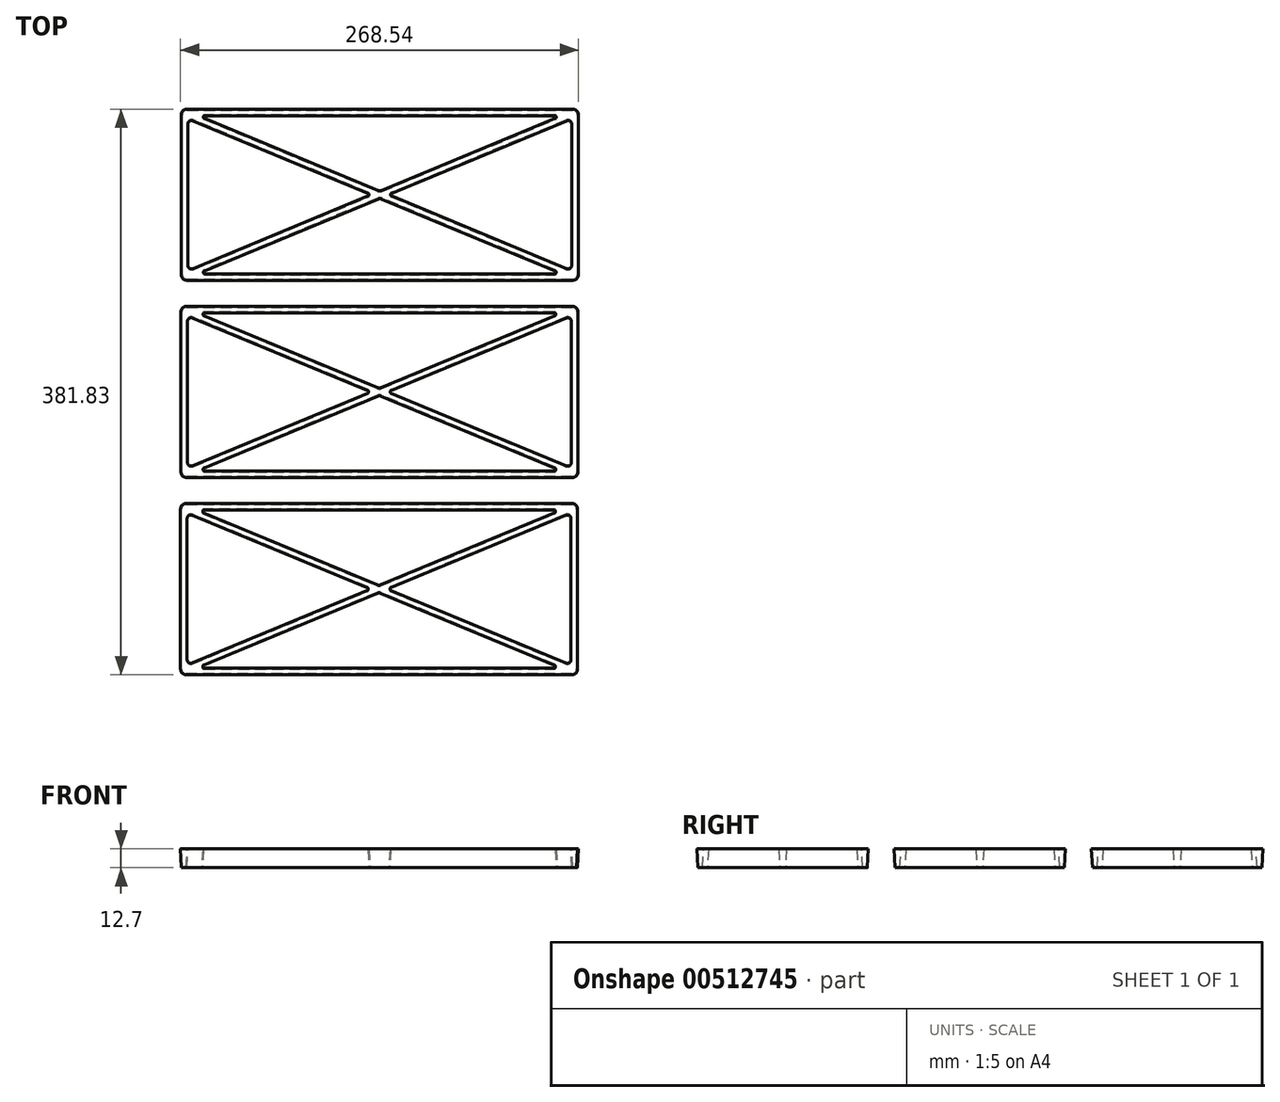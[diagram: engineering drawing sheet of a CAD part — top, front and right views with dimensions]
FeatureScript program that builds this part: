
annotation { "Feature Type Name" : "Feature", "Feature Type Description" : "" }
export const myFeature = defineFeature(function(context is Context, id is Id, definition is map)
    precondition{}
    {
        {
            var Q0;
            Q0=qCreatedBy(makeId("Top.planeOp"),FACE);
            var sketch = newSketch(context, id + "F0", { "sketchPlane" : qUnion([Q0])});
            skLineSegment(sketch, "E0.bottom", {"start": v(-3.18, 0) * mm, "end": v(-263.53, 0) * mm});
            skLineSegment(sketch, "E0.top", {"start": v(-3.18, 114.3) * mm, "end": v(-263.53, 114.3) * mm});
            skLineSegment(sketch, "E0.left", {"start": v(0, 3.17) * mm, "end": v(0, 111.13) * mm});
            skLineSegment(sketch, "E0.right", {"start": v(-266.7, 3.18) * mm, "end": v(-266.7, 111.12) * mm});
            skLineSegment(sketch, "E1.0", {"start": v(-15.3, 111.13) * mm, "end": v(-251.4, 111.13) * mm});
            skLineSegment(sketch, "E2.0", {"start": v(-263.53, 9.65) * mm, "end": v(-263.53, 104.65) * mm});
            skLineSegment(sketch, "E3.0", {"start": v(-15.3, 3.18) * mm, "end": v(-251.4, 3.17) * mm});
            skLineSegment(sketch, "E4.0", {"start": v(-3.18, 9.65) * mm, "end": v(-3.18, 104.65) * mm});
            skLineSegment(sketch, "E5", {"start": v(-263.53, 111.13) * mm, "end": v(-3.18, 3.18) * mm});
            skLineSegment(sketch, "E6", {"start": v(-3.17, 111.13) * mm, "end": v(-263.53, 3.17) * mm});
            skLineSegment(sketch, "E7.0", {"start": v(-132.13, 54.93) * mm, "end": v(-14.69, 6.23) * mm});
            skLineSegment(sketch, "E8.0", {"start": v(-252.01, 108.07) * mm, "end": v(-134.57, 59.37) * mm});
            skLineSegment(sketch, "E9.0", {"start": v(-14.69, 108.07) * mm, "end": v(-132.13, 59.37) * mm});
            skLineSegment(sketch, "E10.0", {"start": v(-134.57, 54.93) * mm, "end": v(-252.01, 6.23) * mm});
            skArc(sketch, "E11.filletArc", {"start": v(-259.13, 107.59) * mm, "mid": v(-262.11, 107.3) * mm, "end": v(-263.53, 104.65) * mm});
            skArc(sketch, "E12.filletArc", {"start": v(-251.4, 111.13) * mm, "mid": v(-252.96, 109.85) * mm, "end": v(-252.01, 108.07) * mm});
            skArc(sketch, "E13.filletArc", {"start": v(-252.01, 6.23) * mm, "mid": v(-252.96, 4.45) * mm, "end": v(-251.4, 3.17) * mm});
            skPoint(sketch, "E14.newPointA", {"position": v(0, 3.18) * mm});
            skArc(sketch, "E14.filletArc", {"start": v(-15.3, 3.18) * mm, "mid": v(-13.74, 4.45) * mm, "end": v(-14.69, 6.23) * mm});
            skArc(sketch, "E15.filletArc", {"start": v(-3.18, 104.65) * mm, "mid": v(-4.59, 107.3) * mm, "end": v(-7.57, 107.59) * mm});
            skPoint(sketch, "E16.newPointB", {"position": v(0, 111.13) * mm});
            skArc(sketch, "E16.filletArc", {"start": v(-14.69, 108.07) * mm, "mid": v(-13.74, 109.85) * mm, "end": v(-15.3, 111.13) * mm});
            skArc(sketch, "E17.filletArc", {"start": v(-263.53, 9.65) * mm, "mid": v(-262.11, 7) * mm, "end": v(-259.13, 6.71) * mm});
            skArc(sketch, "E18.filletArc", {"start": v(-7.57, 6.71) * mm, "mid": v(-4.59, 7) * mm, "end": v(-3.18, 9.65) * mm});
            skArc(sketch, "E19.filletArc", {"start": v(-132.13, 54.93) * mm, "mid": v(-133.35, 55.17) * mm, "end": v(-134.57, 54.93) * mm});
            skArc(sketch, "E20.filletArc", {"start": v(-134.57, 59.37) * mm, "mid": v(-133.35, 59.13) * mm, "end": v(-132.13, 59.37) * mm});
            skLineSegment(sketch, "E21", {"start": v(-259.13, 107.59) * mm, "end": v(-141.03, 58.62) * mm});
            skLineSegment(sketch, "E22", {"start": v(-7.57, 107.59) * mm, "end": v(-125.67, 58.62) * mm});
            skLineSegment(sketch, "E23", {"start": v(-125.67, 55.68) * mm, "end": v(-7.57, 6.71) * mm});
            skLineSegment(sketch, "E24", {"start": v(-259.13, 6.71) * mm, "end": v(-141.03, 55.68) * mm});
            skArc(sketch, "E25.filletArc", {"start": v(-141.03, 55.68) * mm, "mid": v(-140.05, 57.15) * mm, "end": v(-141.03, 58.62) * mm});
            skArc(sketch, "E26.filletArc", {"start": v(-125.67, 58.62) * mm, "mid": v(-126.65, 57.15) * mm, "end": v(-125.67, 55.68) * mm});
            skPoint(sketch, "E27.visualSharp", {"position": v(-266.7, 114.3) * mm});
            skArc(sketch, "E27.filletArc", {"start": v(-263.53, 114.3) * mm, "mid": v(-265.77, 113.37) * mm, "end": v(-266.7, 111.12) * mm});
            skPoint(sketch, "E28.visualSharp", {"position": v(0, 114.3) * mm});
            skArc(sketch, "E28.filletArc", {"start": v(0, 111.13) * mm, "mid": v(-0.93, 113.37) * mm, "end": v(-3.18, 114.3) * mm});
            skPoint(sketch, "E29.visualSharp", {"position": v(0, 0) * mm});
            skArc(sketch, "E29.filletArc", {"start": v(-3.18, 0) * mm, "mid": v(-0.93, 0.93) * mm, "end": v(0, 3.17) * mm});
            skPoint(sketch, "E30.visualSharp", {"position": v(-266.7, 0) * mm});
            skArc(sketch, "E30.filletArc", {"start": v(-266.7, 3.18) * mm, "mid": v(-265.77, 0.93) * mm, "end": v(-263.53, 0) * mm});
            skLineSegment(sketch, "E31.1.0.0", {"start": v(-3.43, -133.1) * mm, "end": v(-263.78, -133.1) * mm});
            skLineSegment(sketch, "E31.1.0.1", {"start": v(-3.43, -18.8) * mm, "end": v(-263.78, -18.8) * mm});
            skLineSegment(sketch, "E31.1.0.2", {"start": v(-259.39, -25.51) * mm, "end": v(-141.29, -74.48) * mm});
            skLineSegment(sketch, "E31.1.0.3", {"start": v(-125.92, -77.41) * mm, "end": v(-7.82, -126.38) * mm});
            skPoint(sketch, "E31.1.0.4", {"position": v(-0.25, -133.1) * mm});
            skLineSegment(sketch, "E31.1.0.5", {"start": v(-259.39, -126.38) * mm, "end": v(-141.29, -77.41) * mm});
            skLineSegment(sketch, "E31.1.0.6", {"start": v(-7.82, -25.51) * mm, "end": v(-125.92, -74.48) * mm});
            skLineSegment(sketch, "E31.1.0.7", {"start": v(-0.25, -129.92) * mm, "end": v(-0.25, -21.97) * mm});
            skLineSegment(sketch, "E31.1.0.8", {"start": v(-132.39, -78.17) * mm, "end": v(-14.94, -126.87) * mm});
            skLineSegment(sketch, "E31.1.0.9", {"start": v(-3.43, -21.97) * mm, "end": v(-263.78, -129.92) * mm});
            skLineSegment(sketch, "E31.1.0.10", {"start": v(-252.27, -25.02) * mm, "end": v(-134.82, -73.72) * mm});
            skLineSegment(sketch, "E31.1.0.11", {"start": v(-266.95, -129.92) * mm, "end": v(-266.95, -21.97) * mm});
            skLineSegment(sketch, "E31.1.0.12", {"start": v(-15.55, -21.97) * mm, "end": v(-251.66, -21.97) * mm});
            skLineSegment(sketch, "E31.1.0.13", {"start": v(-15.55, -129.92) * mm, "end": v(-251.66, -129.92) * mm});
            skPoint(sketch, "E31.1.0.14", {"position": v(-266.95, -133.1) * mm});
            skLineSegment(sketch, "E31.1.0.15", {"start": v(-263.78, -123.45) * mm, "end": v(-263.78, -28.44) * mm});
            skLineSegment(sketch, "E31.1.0.16", {"start": v(-134.82, -78.17) * mm, "end": v(-252.27, -126.87) * mm});
            skLineSegment(sketch, "E31.1.0.17", {"start": v(-3.43, -123.45) * mm, "end": v(-3.43, -28.44) * mm});
            skLineSegment(sketch, "E31.1.0.18", {"start": v(-263.78, -21.97) * mm, "end": v(-3.43, -129.92) * mm});
            skLineSegment(sketch, "E31.1.0.19", {"start": v(-14.94, -25.02) * mm, "end": v(-132.39, -73.72) * mm});
            skPoint(sketch, "E31.1.0.20", {"position": v(-266.95, -18.8) * mm});
            skPoint(sketch, "E31.1.0.21", {"position": v(-0.25, -18.8) * mm});
            skPoint(sketch, "E31.1.0.22", {"position": v(-0.25, -21.97) * mm});
            skPoint(sketch, "E31.1.0.23", {"position": v(-0.25, -129.92) * mm});
            skArc(sketch, "E31.1.0.24", {"start": v(-251.66, -21.97) * mm, "mid": v(-253.22, -23.25) * mm, "end": v(-252.27, -25.02) * mm});
            skArc(sketch, "E31.1.0.25", {"start": v(-259.39, -25.51) * mm, "mid": v(-262.37, -25.8) * mm, "end": v(-263.78, -28.44) * mm});
            skArc(sketch, "E31.1.0.26", {"start": v(-7.82, -126.38) * mm, "mid": v(-4.84, -126.09) * mm, "end": v(-3.43, -123.45) * mm});
            skArc(sketch, "E31.1.0.27", {"start": v(-14.94, -25.02) * mm, "mid": v(-14, -23.25) * mm, "end": v(-15.55, -21.97) * mm});
            skArc(sketch, "E31.1.0.28", {"start": v(-3.43, -28.44) * mm, "mid": v(-4.84, -25.8) * mm, "end": v(-7.82, -25.51) * mm});
            skArc(sketch, "E31.1.0.29", {"start": v(-252.27, -126.87) * mm, "mid": v(-253.22, -128.64) * mm, "end": v(-251.66, -129.92) * mm});
            skArc(sketch, "E31.1.0.30", {"start": v(-266.95, -129.92) * mm, "mid": v(-266.02, -132.17) * mm, "end": v(-263.78, -133.1) * mm});
            skArc(sketch, "E31.1.0.31", {"start": v(-263.78, -123.45) * mm, "mid": v(-262.37, -126.09) * mm, "end": v(-259.39, -126.38) * mm});
            skArc(sketch, "E31.1.0.32", {"start": v(-15.55, -129.92) * mm, "mid": v(-14, -128.64) * mm, "end": v(-14.94, -126.87) * mm});
            skArc(sketch, "E31.1.0.33", {"start": v(-0.25, -21.97) * mm, "mid": v(-1.18, -19.73) * mm, "end": v(-3.43, -18.8) * mm});
            skArc(sketch, "E31.1.0.34", {"start": v(-134.82, -73.72) * mm, "mid": v(-133.6, -73.97) * mm, "end": v(-132.39, -73.72) * mm});
            skArc(sketch, "E31.1.0.35", {"start": v(-125.92, -74.48) * mm, "mid": v(-126.9, -75.95) * mm, "end": v(-125.92, -77.41) * mm});
            skArc(sketch, "E31.1.0.36", {"start": v(-3.43, -133.1) * mm, "mid": v(-1.18, -132.17) * mm, "end": v(-0.25, -129.92) * mm});
            skArc(sketch, "E31.1.0.37", {"start": v(-263.78, -18.8) * mm, "mid": v(-266.02, -19.73) * mm, "end": v(-266.95, -21.97) * mm});
            skArc(sketch, "E31.1.0.38", {"start": v(-132.39, -78.17) * mm, "mid": v(-133.6, -77.93) * mm, "end": v(-134.82, -78.17) * mm});
            skArc(sketch, "E31.1.0.39", {"start": v(-141.29, -77.41) * mm, "mid": v(-140.3, -75.95) * mm, "end": v(-141.29, -74.48) * mm});
            skLineSegment(sketch, "E31.2.0.0", {"start": v(-3.68, -266.2) * mm, "end": v(-264.03, -266.2) * mm});
            skLineSegment(sketch, "E31.2.0.1", {"start": v(-3.68, -151.9) * mm, "end": v(-264.03, -151.9) * mm});
            skLineSegment(sketch, "E31.2.0.2", {"start": v(-259.64, -158.6) * mm, "end": v(-141.54, -207.58) * mm});
            skLineSegment(sketch, "E31.2.0.3", {"start": v(-126.18, -210.5) * mm, "end": v(-8.07, -259.48) * mm});
            skPoint(sketch, "E31.2.0.4", {"position": v(-0.5, -266.2) * mm});
            skLineSegment(sketch, "E31.2.0.5", {"start": v(-259.64, -259.48) * mm, "end": v(-141.54, -210.5) * mm});
            skLineSegment(sketch, "E31.2.0.6", {"start": v(-8.07, -158.6) * mm, "end": v(-126.18, -207.58) * mm});
            skLineSegment(sketch, "E31.2.0.7", {"start": v(-0.5, -263.02) * mm, "end": v(-0.5, -155.07) * mm});
            skLineSegment(sketch, "E31.2.0.8", {"start": v(-132.64, -211.26) * mm, "end": v(-15.2, -259.96) * mm});
            skLineSegment(sketch, "E31.2.0.9", {"start": v(-3.68, -155.07) * mm, "end": v(-264.03, -263.02) * mm});
            skLineSegment(sketch, "E31.2.0.10", {"start": v(-252.52, -158.12) * mm, "end": v(-135.07, -206.82) * mm});
            skLineSegment(sketch, "E31.2.0.11", {"start": v(-267.2, -263.02) * mm, "end": v(-267.2, -155.07) * mm});
            skLineSegment(sketch, "E31.2.0.12", {"start": v(-15.8, -155.07) * mm, "end": v(-251.91, -155.07) * mm});
            skLineSegment(sketch, "E31.2.0.13", {"start": v(-15.8, -263.02) * mm, "end": v(-251.91, -263.02) * mm});
            skPoint(sketch, "E31.2.0.14", {"position": v(-267.2, -266.2) * mm});
            skLineSegment(sketch, "E31.2.0.15", {"start": v(-264.03, -256.54) * mm, "end": v(-264.03, -161.54) * mm});
            skLineSegment(sketch, "E31.2.0.16", {"start": v(-135.07, -211.26) * mm, "end": v(-252.52, -259.96) * mm});
            skLineSegment(sketch, "E31.2.0.17", {"start": v(-3.68, -256.54) * mm, "end": v(-3.68, -161.54) * mm});
            skLineSegment(sketch, "E31.2.0.18", {"start": v(-264.03, -155.07) * mm, "end": v(-3.68, -263.02) * mm});
            skLineSegment(sketch, "E31.2.0.19", {"start": v(-15.2, -158.12) * mm, "end": v(-132.64, -206.82) * mm});
            skPoint(sketch, "E31.2.0.20", {"position": v(-267.2, -151.9) * mm});
            skPoint(sketch, "E31.2.0.21", {"position": v(-0.5, -151.9) * mm});
            skPoint(sketch, "E31.2.0.22", {"position": v(-0.5, -155.07) * mm});
            skPoint(sketch, "E31.2.0.23", {"position": v(-0.5, -263.02) * mm});
            skArc(sketch, "E31.2.0.24", {"start": v(-251.91, -155.07) * mm, "mid": v(-253.47, -156.34) * mm, "end": v(-252.52, -158.12) * mm});
            skArc(sketch, "E31.2.0.25", {"start": v(-259.64, -158.6) * mm, "mid": v(-262.62, -158.9) * mm, "end": v(-264.03, -161.54) * mm});
            skArc(sketch, "E31.2.0.26", {"start": v(-8.07, -259.48) * mm, "mid": v(-5.1, -259.19) * mm, "end": v(-3.68, -256.54) * mm});
            skArc(sketch, "E31.2.0.27", {"start": v(-15.2, -158.12) * mm, "mid": v(-14.24, -156.34) * mm, "end": v(-15.8, -155.07) * mm});
            skArc(sketch, "E31.2.0.28", {"start": v(-3.68, -161.54) * mm, "mid": v(-5.1, -158.9) * mm, "end": v(-8.07, -158.6) * mm});
            skArc(sketch, "E31.2.0.29", {"start": v(-252.52, -259.96) * mm, "mid": v(-253.47, -261.74) * mm, "end": v(-251.91, -263.02) * mm});
            skArc(sketch, "E31.2.0.30", {"start": v(-267.2, -263.02) * mm, "mid": v(-266.28, -265.26) * mm, "end": v(-264.03, -266.2) * mm});
            skArc(sketch, "E31.2.0.31", {"start": v(-264.03, -256.54) * mm, "mid": v(-262.62, -259.19) * mm, "end": v(-259.64, -259.48) * mm});
            skArc(sketch, "E31.2.0.32", {"start": v(-15.8, -263.02) * mm, "mid": v(-14.24, -261.74) * mm, "end": v(-15.2, -259.96) * mm});
            skArc(sketch, "E31.2.0.33", {"start": v(-0.5, -155.07) * mm, "mid": v(-1.44, -152.82) * mm, "end": v(-3.68, -151.9) * mm});
            skArc(sketch, "E31.2.0.34", {"start": v(-135.07, -206.82) * mm, "mid": v(-133.86, -207.06) * mm, "end": v(-132.64, -206.82) * mm});
            skArc(sketch, "E31.2.0.35", {"start": v(-126.18, -207.58) * mm, "mid": v(-127.16, -209.04) * mm, "end": v(-126.18, -210.5) * mm});
            skArc(sketch, "E31.2.0.36", {"start": v(-3.68, -266.2) * mm, "mid": v(-1.44, -265.26) * mm, "end": v(-0.5, -263.02) * mm});
            skArc(sketch, "E31.2.0.37", {"start": v(-264.03, -151.9) * mm, "mid": v(-266.28, -152.82) * mm, "end": v(-267.2, -155.07) * mm});
            skArc(sketch, "E31.2.0.38", {"start": v(-132.64, -211.26) * mm, "mid": v(-133.86, -211.02) * mm, "end": v(-135.07, -211.26) * mm});
            skArc(sketch, "E31.2.0.39", {"start": v(-141.54, -210.5) * mm, "mid": v(-140.56, -209.04) * mm, "end": v(-141.54, -207.58) * mm});
            skLineSegment(sketch, "E31.direction1", {"start": v(-266.7, 0) * mm, "end": v(-266.95, -133.1) * mm, "construction": true});
            skSolve(sketch);
        }
        {
            var Q0;
            Q0 = qSketchRegion(id + "F0", true);
            extrude(context, id + "F1", {"entities" : qUnion([Q0]), "depth" : 12.7 * mm, "offsetDistance" : 25.4 * mm, "hasDraft" : true, "draftAngle" : 3 * degree});
        }
    });
